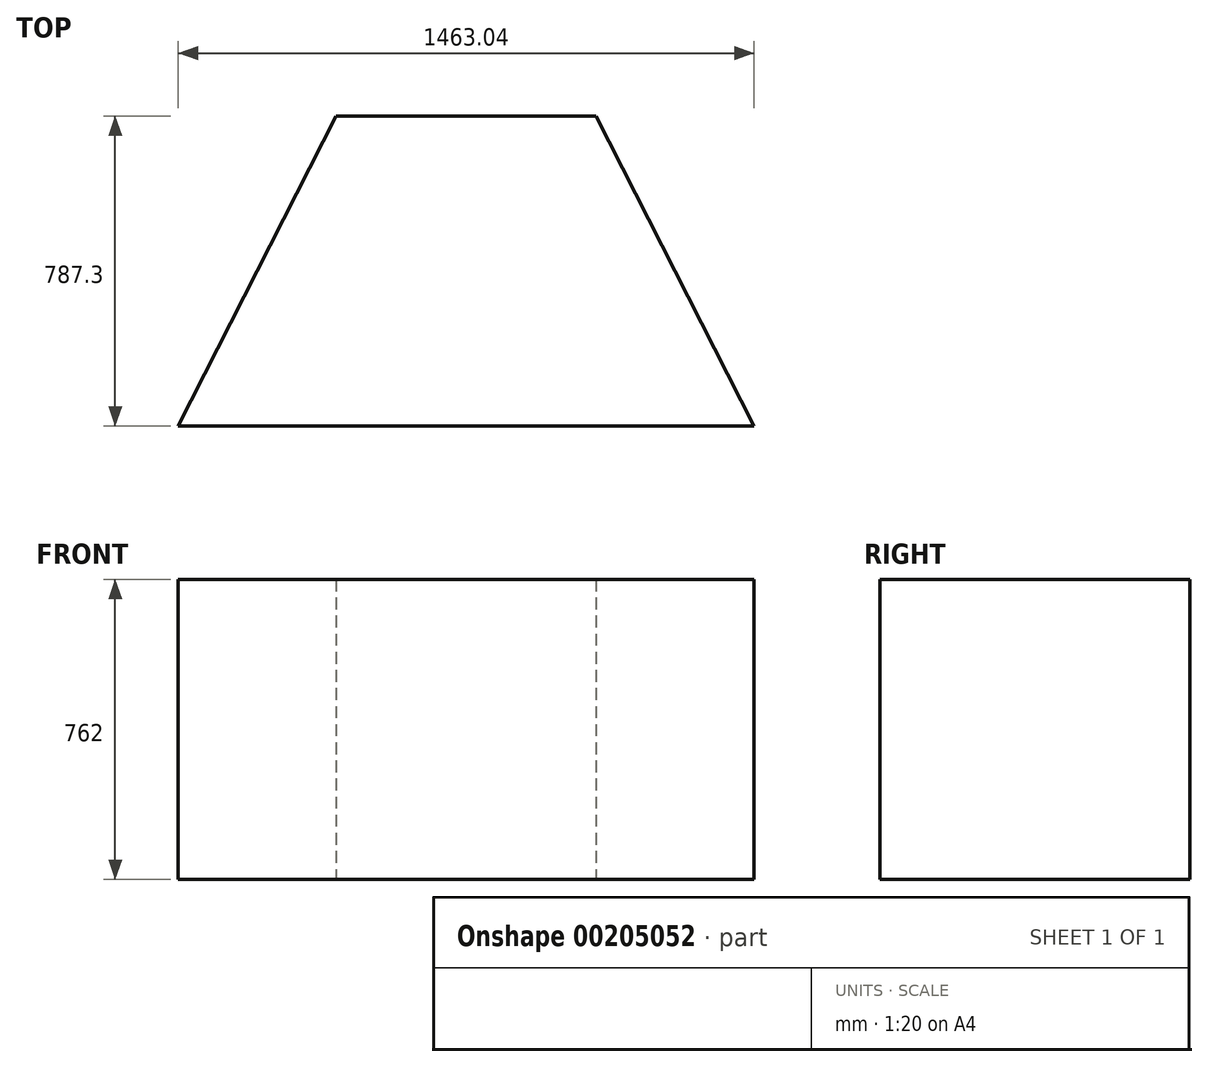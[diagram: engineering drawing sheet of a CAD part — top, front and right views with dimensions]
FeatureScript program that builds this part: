
annotation { "Feature Type Name" : "Feature", "Feature Type Description" : "" }
export const myFeature = defineFeature(function(context is Context, id is Id, definition is map)
    precondition{}
    {
        {
            var Q0;
            Q0=qCreatedBy(makeId("Top.planeOp"),FACE);
            var sketch = newSketch(context, id + "F0", { "sketchPlane" : qUnion([Q0])});
            skLineSegment(sketch, "E0", {"start": v(-731.52, 0) * mm, "end": v(0, 0) * mm});
            skLineSegment(sketch, "E1", {"start": v(0, 0) * mm, "end": v(0, 787.3) * mm});
            skLineSegment(sketch, "E2", {"start": v(0, 787.3) * mm, "end": v(-330.1, 787.3) * mm});
            skLineSegment(sketch, "E3", {"start": v(-330.1, 787.3) * mm, "end": v(-731.52, 0) * mm});
            skPoint(sketch, "E4.MirrorCS.start.orphan", {"position": v(0, 787.3) * mm});
            skLineSegment(sketch, "E5.MirrorCS", {"start": v(731.52, 0) * mm, "end": v(0, 0) * mm});
            skLineSegment(sketch, "E6.MirrorCS", {"start": v(330.1, 787.3) * mm, "end": v(731.52, 0) * mm});
            skLineSegment(sketch, "E7.MirrorCS", {"start": v(0, 787.3) * mm, "end": v(330.1, 787.3) * mm});
            skSolve(sketch);
        }
        {
            var Q0;
            Q0=makeQuery(id+"F0.imprint","IMPRINT",FACE,{"disambiguationData":[TD([[makeQuery(id+"F0.imprint","IMPRINT",EDGE,{"derivedFrom":sQuery(id+"F0.wireOp",EDGE,"E0")}),1.0]])]});
            var Q1;
            Q1=makeQuery(id+"F0.imprint","IMPRINT",FACE,{"disambiguationData":[TD([[makeQuery(id+"F0.imprint","IMPRINT",EDGE,{"derivedFrom":sQuery(id+"F0.wireOp",EDGE,"E1")}),-1.0]])]});
            extrude(context, id + "F1", {"entities" : qUnion([Q0, Q1]), "depth" : 762 * mm});
        }
    });
